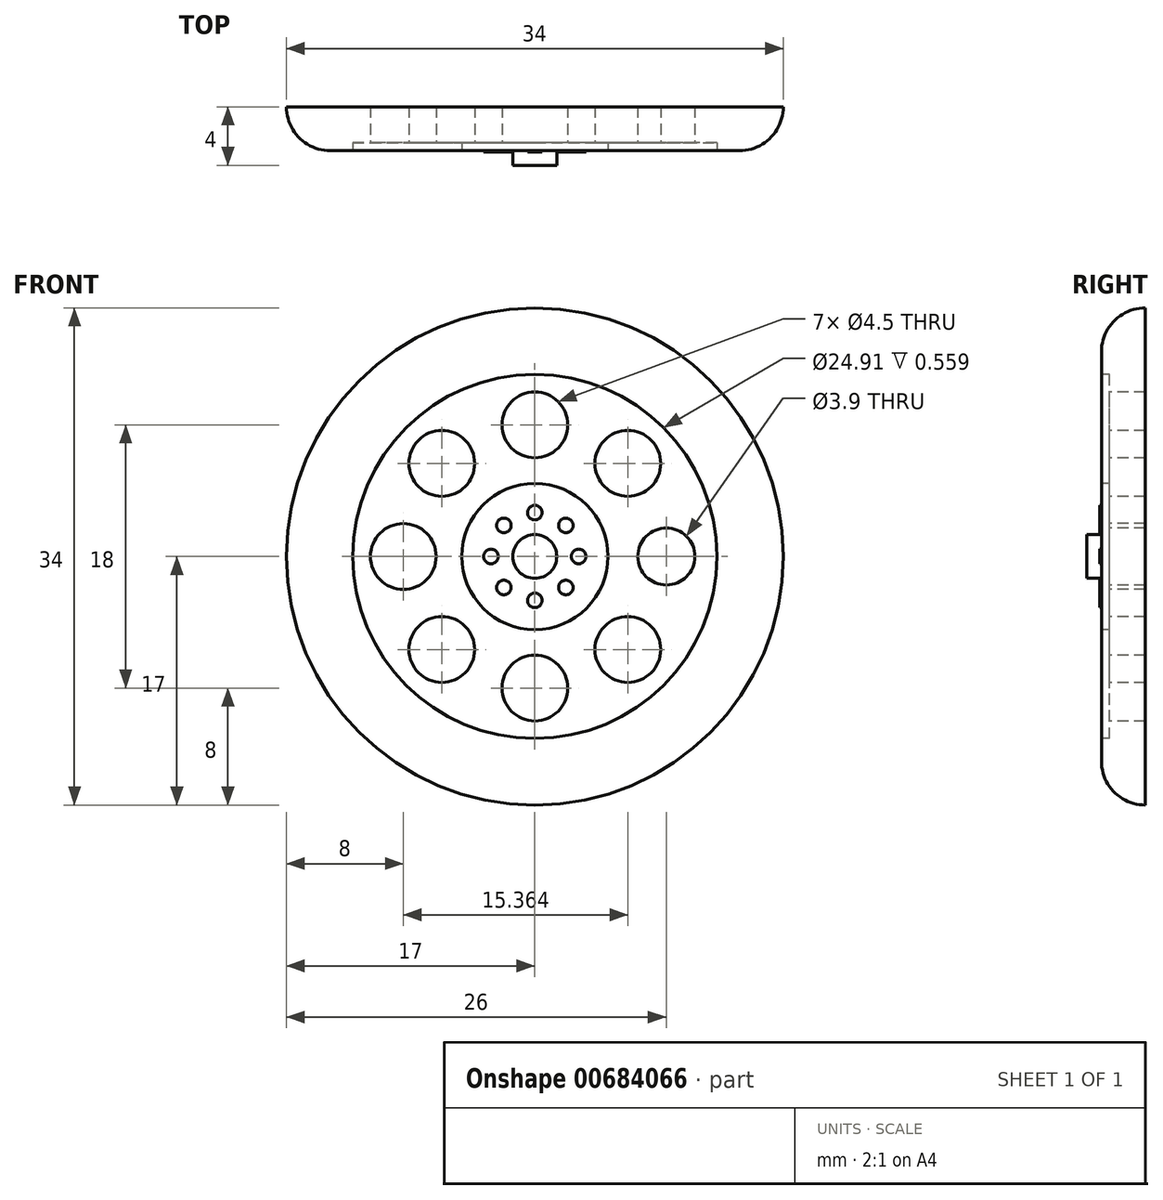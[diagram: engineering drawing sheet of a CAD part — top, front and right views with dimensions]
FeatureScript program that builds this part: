
annotation { "Feature Type Name" : "Feature", "Feature Type Description" : "" }
export const myFeature = defineFeature(function(context is Context, id is Id, definition is map)
    precondition{}
    {
        {
            var Q0;
            Q0=qCreatedBy(makeId("Front.planeOp"),FACE);
            var sketch = newSketch(context, id + "F0", { "sketchPlane" : qUnion([Q0])});
            skCircle(sketch, "E0", {"center": v(0, 0) * mm, "radius": 17 * mm});
            skSolve(sketch);
        }
        {
            var Q0;
            Q0=makeQuery(id+"F0.imprint","IMPRINT",FACE,{"disambiguationData":[TD([[makeQuery(id+"F0.imprint","IMPRINT",EDGE,{"derivedFrom":sQuery(id+"F0.wireOp",EDGE,"E0")}),1.0]])]});
            extrude(context, id + "F1", {"entities" : qUnion([Q0]), "depth" : 3 * mm, "offsetDistance" : 25.4 * mm});
        }
        {
            var Q0;
            Q0=makeQuery(id+"F1.opExtrude","CAP_FACE",FACE,{"disambiguationData":[OSD([sQuery(id+"F0.wireOp",EDGE,"E0")])],"isStart":false});
            var sketch = newSketch(context, id + "F2", { "sketchPlane" : qUnion([Q0])});
            skCircle(sketch, "E1", {"center": v(0, 0) * mm, "radius": 14 * mm});
            skSolve(sketch);
        }
        {
            var Q0;
            Q0=makeQuery(id+"F1.opExtrude","CAP_FACE",FACE,{"disambiguationData":[OSD([sQuery(id+"F0.wireOp",EDGE,"E0")])],"isStart":false});
            fillet(context, id + "F3", {"entities" : qUnion([Q0]), "radius" : 3 * mm, "tangentPropagation" : true, "allowEdgeOverflow" : false});
        }
        {
            var Q0;
            Q0=makeQuery(id+"F2.imprint","IMPRINT",FACE,{"disambiguationData":[TD([[makeQuery(id+"F2.imprint","IMPRINT",EDGE,{"derivedFrom":sQuery(id+"F2.wireOp",EDGE,"E1")}),1.0]])]});
            var sketch = newSketch(context, id + "F4", { "sketchPlane" : qUnion([Q0])});
            skCircle(sketch, "E2", {"center": v(0, 0) * mm, "radius": 12.5 * mm});
            skSolve(sketch);
        }
        {
            var Q0;
            Q0=makeQuery(id+"F2.imprint","IMPRINT",FACE,{"disambiguationData":[TD([[makeQuery(id+"F2.imprint","IMPRINT",EDGE,{"derivedFrom":sQuery(id+"F2.wireOp",EDGE,"E1")}),1.0]])]});
            var sketch = newSketch(context, id + "F5", { "sketchPlane" : qUnion([Q0])});
            skCircle(sketch, "E3", {"center": v(0, 0) * mm, "radius": 12.45 * mm});
            skSolve(sketch);
        }
        {
            var Q0;
            Q0=makeQuery(id+"F5.imprint","IMPRINT",FACE,{"disambiguationData":[TD([[makeQuery(id+"F5.imprint","IMPRINT",EDGE,{"derivedFrom":sQuery(id+"F5.wireOp",EDGE,"E3")}),1.0]])]});
            extrude(context, id + "F6", {"entities" : qUnion([Q0]), "operationType" : NewBodyOperationType.REMOVE, "oppositeDirection" : true, "depth" : 0.56 * mm, "offsetDistance" : 25.4 * mm});
        }
        {
            var Q0;
            Q0=makeQuery(id+"F4.imprint","IMPRINT",FACE,{"disambiguationData":[TD([[makeQuery(id+"F4.imprint","IMPRINT",EDGE,{"derivedFrom":sQuery(id+"F4.wireOp",EDGE,"E2")}),1.0]])]});
            var sketch = newSketch(context, id + "F7", { "sketchPlane" : qUnion([Q0])});
            skCircle(sketch, "E4", {"center": v(0, 0) * mm, "radius": 5 * mm});
            skSolve(sketch);
        }
        {
            var Q0;
            Q0 = qSketchRegion(id + "F7", true);
            extrude(context, id + "F8", {"entities" : qUnion([Q0]), "operationType" : NewBodyOperationType.ADD, "oppositeDirection" : true, "depth" : 1.14 * mm, "offsetDistance" : 25.4 * mm});
        }
        {
            var Q0;
            Q0=makeQuery(id+"F2.imprint","IMPRINT",FACE,{"disambiguationData":[TD([[makeQuery(id+"F2.imprint","IMPRINT",EDGE,{"derivedFrom":sQuery(id+"F2.wireOp",EDGE,"E1")}),1.0]])]});
            var sketch = newSketch(context, id + "F9", { "sketchPlane" : qUnion([Q0])});
            skLineSegment(sketch, "E5", {"start": v(0, 9) * mm, "end": v(0, -9) * mm});
            skLineSegment(sketch, "E6", {"start": v(-9, 0) * mm, "end": v(9, 0) * mm});
            skLineSegment(sketch, "E7", {"start": v(0, 0) * mm, "end": v(-6.36, 6.36) * mm});
            skLineSegment(sketch, "E8", {"start": v(0, 0) * mm, "end": v(6.36, 6.36) * mm});
            skLineSegment(sketch, "E9", {"start": v(0, 0) * mm, "end": v(-6.36, -6.36) * mm});
            skLineSegment(sketch, "E10", {"start": v(0, 0) * mm, "end": v(6.36, -6.36) * mm});
            skSolve(sketch);
        }
        {
            var Q0;
            Q0=makeQuery(id+"F2.imprint","IMPRINT",FACE,{"disambiguationData":[TD([[makeQuery(id+"F2.imprint","IMPRINT",EDGE,{"derivedFrom":sQuery(id+"F2.wireOp",EDGE,"E1")}),1.0]])]});
            var sketch = newSketch(context, id + "F10", { "sketchPlane" : qUnion([Q0])});
            skLineSegment(sketch, "E11.0", {"start": v(0, 9) * mm, "end": v(0, -9) * mm});
            skLineSegment(sketch, "E12.0", {"start": v(0, 0) * mm, "end": v(-6.36, 6.36) * mm});
            skLineSegment(sketch, "E13.0", {"start": v(0, 0) * mm, "end": v(6.36, 6.36) * mm});
            skLineSegment(sketch, "E14.0", {"start": v(-9, 0) * mm, "end": v(9, 0) * mm});
            skLineSegment(sketch, "E15.0", {"start": v(0, 0) * mm, "end": v(6.36, -6.36) * mm});
            skLineSegment(sketch, "E16.0", {"start": v(0, 0) * mm, "end": v(-6.36, -6.36) * mm});
            skCircle(sketch, "E17", {"center": v(0, 9) * mm, "radius": 2.25 * mm});
            skCircle(sketch, "E18", {"center": v(6.36, 6.36) * mm, "radius": 2.25 * mm});
            skCircle(sketch, "E19", {"center": v(9, 0) * mm, "radius": 1.95 * mm});
            skCircle(sketch, "E20", {"center": v(6.36, -6.36) * mm, "radius": 2.25 * mm});
            skCircle(sketch, "E21", {"center": v(0, -9) * mm, "radius": 2.25 * mm});
            skCircle(sketch, "E22", {"center": v(-6.36, -6.36) * mm, "radius": 2.25 * mm});
            skCircle(sketch, "E23", {"center": v(-9, 0) * mm, "radius": 2.25 * mm});
            skCircle(sketch, "E24", {"center": v(-6.36, 6.36) * mm, "radius": 2.25 * mm});
            skSolve(sketch);
        }
        {
            var Q0;
            Q0=makeQuery(id+"F10.imprint","IMPRINT",FACE,{"disambiguationData":[TD([[makeQuery(id+"F10.imprint","IMPRINT",EDGE,{"derivedFrom":sQuery(id+"F10.wireOp",EDGE,"E20")}),1.0]])]});
            var Q1;
            Q1=makeQuery(id+"F10.imprint","IMPRINT",FACE,{"disambiguationData":[TD([[makeQuery(id+"F10.imprint","IMPRINT",EDGE,{"derivedFrom":sQuery(id+"F10.wireOp",EDGE,"E21")}),1.0]])]});
            var Q2;
            Q2=makeQuery(id+"F10.imprint","IMPRINT",FACE,{"disambiguationData":[TD([[makeQuery(id+"F10.imprint","IMPRINT",EDGE,{"derivedFrom":sQuery(id+"F10.wireOp",EDGE,"E22")}),1.0]])]});
            var Q3;
            Q3=makeQuery(id+"F10.imprint","IMPRINT",FACE,{"disambiguationData":[TD([[makeQuery(id+"F10.imprint","IMPRINT",EDGE,{"derivedFrom":sQuery(id+"F10.wireOp",EDGE,"E19")}),1.0]])]});
            var Q4;
            Q4=makeQuery(id+"F10.imprint","IMPRINT",FACE,{"disambiguationData":[TD([[makeQuery(id+"F10.imprint","IMPRINT",EDGE,{"derivedFrom":sQuery(id+"F10.wireOp",EDGE,"E23")}),1.0]])]});
            var Q5;
            Q5=makeQuery(id+"F10.imprint","IMPRINT",FACE,{"disambiguationData":[TD([[makeQuery(id+"F10.imprint","IMPRINT",EDGE,{"derivedFrom":sQuery(id+"F10.wireOp",EDGE,"E24")}),1.0]])]});
            var Q6;
            Q6=makeQuery(id+"F10.imprint","IMPRINT",FACE,{"disambiguationData":[TD([[makeQuery(id+"F10.imprint","IMPRINT",EDGE,{"derivedFrom":sQuery(id+"F10.wireOp",EDGE,"E17")}),1.0]])]});
            var Q7;
            Q7=makeQuery(id+"F10.imprint","IMPRINT",FACE,{"disambiguationData":[TD([[makeQuery(id+"F10.imprint","IMPRINT",EDGE,{"derivedFrom":sQuery(id+"F10.wireOp",EDGE,"E18")}),1.0]])]});
            extrude(context, id + "F11", {"entities" : qUnion([Q0, Q1, Q2, Q3, Q4, Q5, Q6, Q7]), "operationType" : NewBodyOperationType.REMOVE, "oppositeDirection" : true, "depth" : 25.4 * mm, "offsetDistance" : 25.4 * mm});
        }
        {
            var Q0;
            Q0=makeQuery(id+"F2.imprint","IMPRINT",FACE,{"disambiguationData":[TD([[makeQuery(id+"F2.imprint","IMPRINT",EDGE,{"derivedFrom":sQuery(id+"F2.wireOp",EDGE,"E1")}),1.0]])]});
            var sketch = newSketch(context, id + "F12", { "sketchPlane" : qUnion([Q0])});
            skLineSegment(sketch, "E25.0", {"start": v(0, 9) * mm, "end": v(0, -9) * mm});
            skLineSegment(sketch, "E26.0", {"start": v(0, 0) * mm, "end": v(6.36, 6.36) * mm});
            skLineSegment(sketch, "E27.0", {"start": v(-9, 0) * mm, "end": v(9, 0) * mm});
            skLineSegment(sketch, "E28.0", {"start": v(0, 0) * mm, "end": v(-6.36, 6.36) * mm});
            skLineSegment(sketch, "E29.0", {"start": v(0, 0) * mm, "end": v(6.36, -6.36) * mm});
            skLineSegment(sketch, "E30.0", {"start": v(0, 0) * mm, "end": v(-6.36, -6.36) * mm});
            skLineSegment(sketch, "E31", {"start": v(0, 0) * mm, "end": v(0, 3) * mm});
            skLineSegment(sketch, "E32", {"start": v(0, 0) * mm, "end": v(2.12, 2.12) * mm});
            skLineSegment(sketch, "E33", {"start": v(0, 0) * mm, "end": v(-2.12, 2.12) * mm});
            skLineSegment(sketch, "E34", {"start": v(0, 0) * mm, "end": v(-2.12, -2.12) * mm});
            skLineSegment(sketch, "E35", {"start": v(0, 0) * mm, "end": v(-3, 0) * mm});
            skLineSegment(sketch, "E36", {"start": v(0, 0) * mm, "end": v(0, -3) * mm});
            skLineSegment(sketch, "E37", {"start": v(0, 0) * mm, "end": v(2.12, -2.12) * mm});
            skLineSegment(sketch, "E38", {"start": v(0, 0) * mm, "end": v(3, 0) * mm});
            skCircle(sketch, "E39", {"center": v(0, 3) * mm, "radius": 0.5 * mm});
            skCircle(sketch, "E40", {"center": v(2.12, 2.12) * mm, "radius": 0.5 * mm});
            skCircle(sketch, "E41", {"center": v(3, 0) * mm, "radius": 0.5 * mm});
            skCircle(sketch, "E42", {"center": v(2.12, -2.12) * mm, "radius": 0.5 * mm});
            skCircle(sketch, "E43", {"center": v(0, -3) * mm, "radius": 0.5 * mm});
            skCircle(sketch, "E44", {"center": v(-2.12, -2.12) * mm, "radius": 0.5 * mm});
            skCircle(sketch, "E45", {"center": v(-3, 0) * mm, "radius": 0.5 * mm});
            skCircle(sketch, "E46", {"center": v(-2.12, 2.12) * mm, "radius": 0.5 * mm});
            skSolve(sketch);
        }
        {
            var Q0;
            {var subQ0=sQuery(id+"F12.wireOp",EDGE,"E33");var subQ1=sQuery(id+"F12.wireOp",EDGE,"E28.0");var subQ2=makeQuery(id+"F12.imprint","INTERSECT",VERTEX,{"derivedFrom":[subQ1,subQ0]});Q0=makeQuery(id+"F12.imprint","IMPRINT",FACE,{"disambiguationData":[TD([[makeQuery(id+"F12.imprint","IMPRINT",EDGE,{"disambiguationData":[TD([[subQ2,-1.0]])],"derivedFrom":subQ1}),-1.0]])]});}
            var Q1;
            {var subQ0=sQuery(id+"F12.wireOp",EDGE,"E33");var subQ1=sQuery(id+"F12.wireOp",EDGE,"E28.0");var subQ2=makeQuery(id+"F12.imprint","INTERSECT",VERTEX,{"derivedFrom":[subQ1,subQ0]});Q1=makeQuery(id+"F12.imprint","IMPRINT",FACE,{"disambiguationData":[TD([[makeQuery(id+"F12.imprint","IMPRINT",EDGE,{"disambiguationData":[TD([[subQ2,-1.0]])],"derivedFrom":subQ1}),1.0]])]});}
            var Q2;
            {var subQ0=sQuery(id+"F12.wireOp",EDGE,"E31");var subQ1=sQuery(id+"F12.wireOp",EDGE,"E25.0");var subQ2=makeQuery(id+"F12.imprint","INTERSECT",VERTEX,{"derivedFrom":[subQ1,subQ0]});Q2=makeQuery(id+"F12.imprint","IMPRINT",FACE,{"disambiguationData":[TD([[makeQuery(id+"F12.imprint","IMPRINT",EDGE,{"disambiguationData":[TD([[subQ2,1.0]])],"derivedFrom":subQ1}),-1.0]])]});}
            var Q3;
            {var subQ0=sQuery(id+"F12.wireOp",EDGE,"E31");var subQ1=sQuery(id+"F12.wireOp",EDGE,"E25.0");var subQ2=makeQuery(id+"F12.imprint","INTERSECT",VERTEX,{"derivedFrom":[subQ1,subQ0]});Q3=makeQuery(id+"F12.imprint","IMPRINT",FACE,{"disambiguationData":[TD([[makeQuery(id+"F12.imprint","IMPRINT",EDGE,{"disambiguationData":[TD([[subQ2,1.0]])],"derivedFrom":subQ1}),1.0]])]});}
            var Q4;
            {var subQ0=sQuery(id+"F12.wireOp",EDGE,"E37");var subQ1=sQuery(id+"F12.wireOp",EDGE,"E29.0");var subQ2=makeQuery(id+"F12.imprint","INTERSECT",VERTEX,{"derivedFrom":[subQ1,subQ0]});Q4=makeQuery(id+"F12.imprint","IMPRINT",FACE,{"disambiguationData":[TD([[makeQuery(id+"F12.imprint","IMPRINT",EDGE,{"disambiguationData":[TD([[subQ2,-1.0]])],"derivedFrom":subQ1}),1.0]])]});}
            var Q5;
            {var subQ0=sQuery(id+"F12.wireOp",EDGE,"E37");var subQ1=sQuery(id+"F12.wireOp",EDGE,"E29.0");var subQ2=makeQuery(id+"F12.imprint","INTERSECT",VERTEX,{"derivedFrom":[subQ1,subQ0]});Q5=makeQuery(id+"F12.imprint","IMPRINT",FACE,{"disambiguationData":[TD([[makeQuery(id+"F12.imprint","IMPRINT",EDGE,{"disambiguationData":[TD([[subQ2,-1.0]])],"derivedFrom":subQ1}),-1.0]])]});}
            var Q6;
            {var subQ0=sQuery(id+"F12.wireOp",EDGE,"E35");var subQ1=sQuery(id+"F12.wireOp",EDGE,"E27.0");var subQ2=makeQuery(id+"F12.imprint","INTERSECT",VERTEX,{"derivedFrom":[subQ1,subQ0]});Q6=makeQuery(id+"F12.imprint","IMPRINT",FACE,{"disambiguationData":[TD([[makeQuery(id+"F12.imprint","IMPRINT",EDGE,{"disambiguationData":[TD([[subQ2,1.0]])],"derivedFrom":subQ1}),-1.0]])]});}
            var Q7;
            {var subQ0=sQuery(id+"F12.wireOp",EDGE,"E35");var subQ1=sQuery(id+"F12.wireOp",EDGE,"E27.0");var subQ2=makeQuery(id+"F12.imprint","INTERSECT",VERTEX,{"derivedFrom":[subQ1,subQ0]});Q7=makeQuery(id+"F12.imprint","IMPRINT",FACE,{"disambiguationData":[TD([[makeQuery(id+"F12.imprint","IMPRINT",EDGE,{"disambiguationData":[TD([[subQ2,1.0]])],"derivedFrom":subQ1}),1.0]])]});}
            var Q8;
            {var subQ0=sQuery(id+"F12.wireOp",EDGE,"E34");var subQ1=sQuery(id+"F12.wireOp",EDGE,"E30.0");var subQ2=makeQuery(id+"F12.imprint","INTERSECT",VERTEX,{"derivedFrom":[subQ1,subQ0]});Q8=makeQuery(id+"F12.imprint","IMPRINT",FACE,{"disambiguationData":[TD([[makeQuery(id+"F12.imprint","IMPRINT",EDGE,{"disambiguationData":[TD([[subQ2,-1.0]])],"derivedFrom":subQ1}),-1.0]])]});}
            var Q9;
            {var subQ0=sQuery(id+"F12.wireOp",EDGE,"E34");var subQ1=sQuery(id+"F12.wireOp",EDGE,"E30.0");var subQ2=makeQuery(id+"F12.imprint","INTERSECT",VERTEX,{"derivedFrom":[subQ1,subQ0]});Q9=makeQuery(id+"F12.imprint","IMPRINT",FACE,{"disambiguationData":[TD([[makeQuery(id+"F12.imprint","IMPRINT",EDGE,{"disambiguationData":[TD([[subQ2,-1.0]])],"derivedFrom":subQ1}),1.0]])]});}
            var Q10;
            {var subQ0=sQuery(id+"F12.wireOp",EDGE,"E36");var subQ1=sQuery(id+"F12.wireOp",EDGE,"E25.0");var subQ2=makeQuery(id+"F12.imprint","INTERSECT",VERTEX,{"derivedFrom":[subQ1,subQ0]});Q10=makeQuery(id+"F12.imprint","IMPRINT",FACE,{"disambiguationData":[TD([[makeQuery(id+"F12.imprint","IMPRINT",EDGE,{"disambiguationData":[TD([[subQ2,-1.0]])],"derivedFrom":subQ1}),1.0]])]});}
            var Q11;
            {var subQ0=sQuery(id+"F12.wireOp",EDGE,"E36");var subQ1=sQuery(id+"F12.wireOp",EDGE,"E25.0");var subQ2=makeQuery(id+"F12.imprint","INTERSECT",VERTEX,{"derivedFrom":[subQ1,subQ0]});Q11=makeQuery(id+"F12.imprint","IMPRINT",FACE,{"disambiguationData":[TD([[makeQuery(id+"F12.imprint","IMPRINT",EDGE,{"disambiguationData":[TD([[subQ2,-1.0]])],"derivedFrom":subQ1}),-1.0]])]});}
            var Q12;
            {var subQ0=sQuery(id+"F12.wireOp",EDGE,"E38");var subQ1=sQuery(id+"F12.wireOp",EDGE,"E27.0");var subQ2=makeQuery(id+"F12.imprint","INTERSECT",VERTEX,{"derivedFrom":[subQ1,subQ0]});Q12=makeQuery(id+"F12.imprint","IMPRINT",FACE,{"disambiguationData":[TD([[makeQuery(id+"F12.imprint","IMPRINT",EDGE,{"disambiguationData":[TD([[subQ2,-1.0]])],"derivedFrom":subQ1}),-1.0]])]});}
            var Q13;
            {var subQ0=sQuery(id+"F12.wireOp",EDGE,"E38");var subQ1=sQuery(id+"F12.wireOp",EDGE,"E27.0");var subQ2=makeQuery(id+"F12.imprint","INTERSECT",VERTEX,{"derivedFrom":[subQ1,subQ0]});Q13=makeQuery(id+"F12.imprint","IMPRINT",FACE,{"disambiguationData":[TD([[makeQuery(id+"F12.imprint","IMPRINT",EDGE,{"disambiguationData":[TD([[subQ2,-1.0]])],"derivedFrom":subQ1}),1.0]])]});}
            var Q14;
            {var subQ0=sQuery(id+"F12.wireOp",EDGE,"E32");var subQ1=sQuery(id+"F12.wireOp",EDGE,"E26.0");var subQ2=makeQuery(id+"F12.imprint","INTERSECT",VERTEX,{"derivedFrom":[subQ1,subQ0]});Q14=makeQuery(id+"F12.imprint","IMPRINT",FACE,{"disambiguationData":[TD([[makeQuery(id+"F12.imprint","IMPRINT",EDGE,{"disambiguationData":[TD([[subQ2,-1.0]])],"derivedFrom":subQ1}),-1.0]])]});}
            var Q15;
            {var subQ0=sQuery(id+"F12.wireOp",EDGE,"E32");var subQ1=sQuery(id+"F12.wireOp",EDGE,"E26.0");var subQ2=makeQuery(id+"F12.imprint","INTERSECT",VERTEX,{"derivedFrom":[subQ1,subQ0]});Q15=makeQuery(id+"F12.imprint","IMPRINT",FACE,{"disambiguationData":[TD([[makeQuery(id+"F12.imprint","IMPRINT",EDGE,{"disambiguationData":[TD([[subQ2,-1.0]])],"derivedFrom":subQ1}),1.0]])]});}
            extrude(context, id + "F13", {"entities" : qUnion([Q0, Q1, Q2, Q3, Q4, Q5, Q6, Q7, Q8, Q9, Q10, Q11, Q12, Q13, Q14, Q15]), "operationType" : NewBodyOperationType.ADD, "depth" : .1 * mm, "offsetDistance" : 25.4 * mm});
        }
        {
            var Q0;
            Q0=makeQuery(id+"F2.imprint","IMPRINT",FACE,{"disambiguationData":[TD([[makeQuery(id+"F2.imprint","IMPRINT",EDGE,{"derivedFrom":sQuery(id+"F2.wireOp",EDGE,"E1")}),1.0]])]});
            var sketch = newSketch(context, id + "F14", { "sketchPlane" : qUnion([Q0])});
            skCircle(sketch, "E47", {"center": v(0, 0) * mm, "radius": 1.5 * mm});
            skSolve(sketch);
        }
        {
            var Q0;
            Q0=makeQuery(id+"F14.imprint","IMPRINT",FACE,{"disambiguationData":[TD([[makeQuery(id+"F14.imprint","IMPRINT",EDGE,{"derivedFrom":sQuery(id+"F14.wireOp",EDGE,"E47")}),1.0]])]});
            extrude(context, id + "F15", {"entities" : qUnion([Q0]), "operationType" : NewBodyOperationType.ADD, "depth" : 1 * mm, "offsetDistance" : 25.4 * mm});
        }
    });
